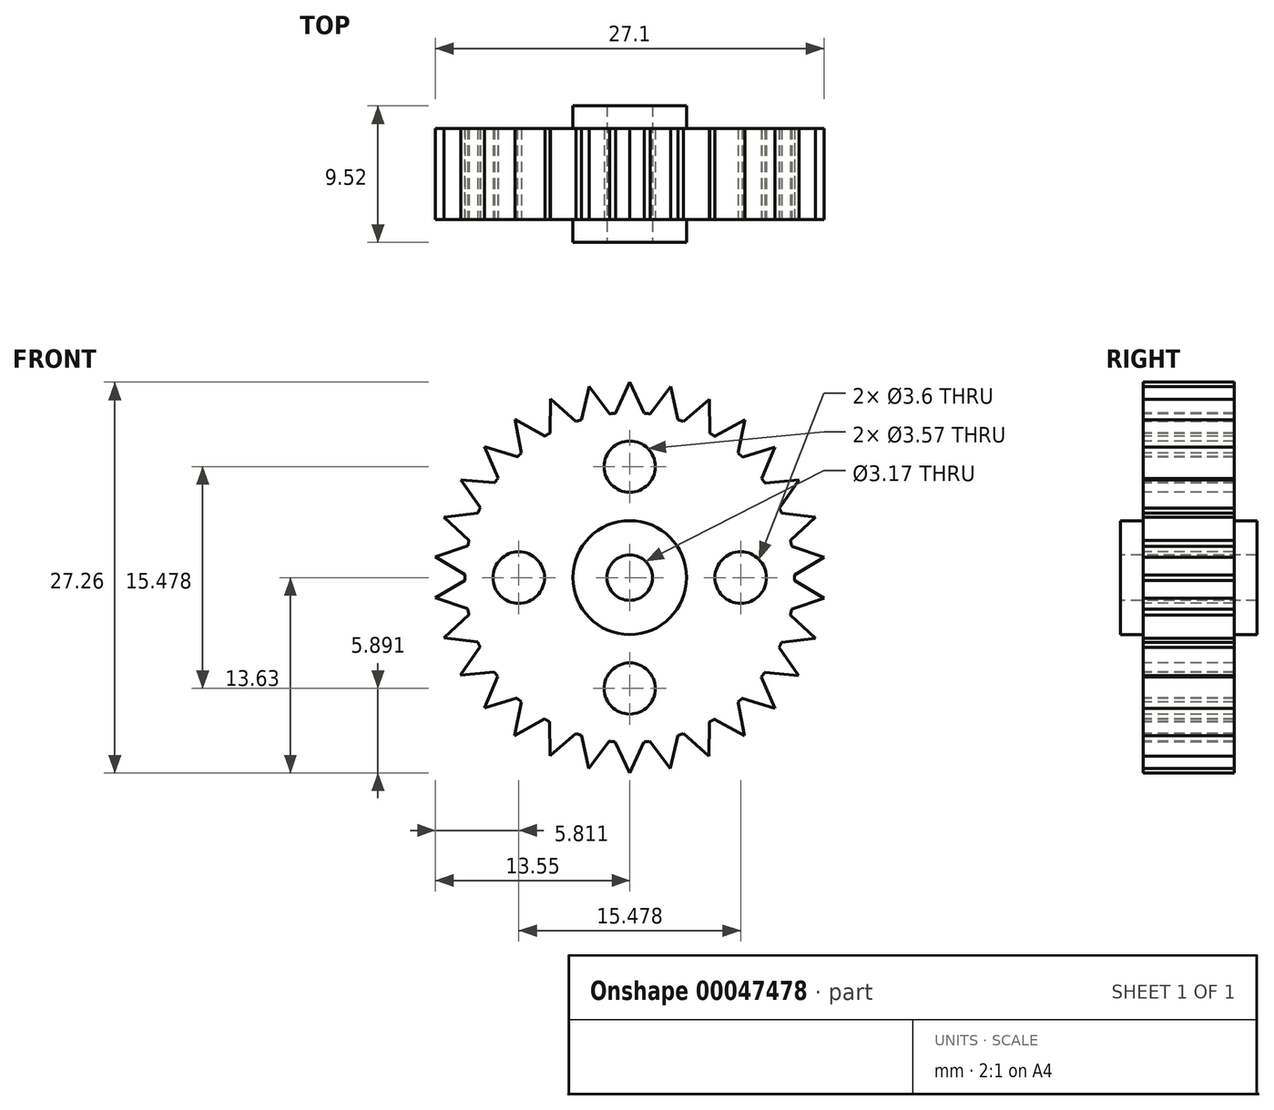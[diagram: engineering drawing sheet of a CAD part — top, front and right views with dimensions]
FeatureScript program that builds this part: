
annotation { "Feature Type Name" : "Feature", "Feature Type Description" : "" }
export const myFeature = defineFeature(function(context is Context, id is Id, definition is map)
    precondition{}
    {
        {
            var Q0;
            Q0=qCreatedBy(makeId("Front.planeOp"),FACE);
            var sketch = newSketch(context, id + "F0", { "sketchPlane" : qUnion([Q0])});
            skCircle(sketch, "E0", {"center": v(0, 0) * mm, "radius": 11.5 * mm});
            skSolve(sketch);
        }
        {
            var Q0;
            Q0=makeQuery(id+"F0.imprint","IMPRINT",FACE,{"disambiguationData":[TD([[makeQuery(id+"F0.imprint","IMPRINT",EDGE,{"derivedFrom":sQuery(id+"F0.wireOp",EDGE,"E0")}),1.0]])]});
            extrude(context, id + "F1", {"entities" : qUnion([Q0]), "depth" : 6.35 * mm, "symmetric" : true});
        }
        {
            var Q0;
            Q0=makeQuery(id+"F1.opExtrude","CAP_FACE",FACE,{"disambiguationData":[OSD([sQuery(id+"F0.wireOp",EDGE,"E0")])],"isStart":false});
            var sketch = newSketch(context, id + "F2", { "sketchPlane" : qUnion([Q0])});
            skCircle(sketch, "E1", {"center": v(0, 0) * mm, "radius": 3.97 * mm});
            skSolve(sketch);
        }
        {
            var Q0;
            Q0=makeQuery(id+"F2.imprint","IMPRINT",FACE,{"disambiguationData":[TD([[makeQuery(id+"F2.imprint","IMPRINT",EDGE,{"derivedFrom":sQuery(id+"F2.wireOp",EDGE,"E1")}),1.0]])]});
            extrude(context, id + "F3", {"entities" : qUnion([Q0]), "operationType" : NewBodyOperationType.ADD, "depth" : 1.59 * mm});
        }
        {
            var Q0;
            Q0=makeQuery(id+"F3.opExtrude","CAP_FACE",FACE,{"disambiguationData":[OSD([sQuery(id+"F2.wireOp",EDGE,"E1")])],"isStart":false});
            var sketch = newSketch(context, id + "F4", { "sketchPlane" : qUnion([Q0])});
            skCircle(sketch, "E2", {"center": v(0, 0) * mm, "radius": 1.59 * mm});
            skSolve(sketch);
        }
        {
            var Q0;
            Q0=makeQuery(id+"F4.imprint","IMPRINT",FACE,{"disambiguationData":[TD([[makeQuery(id+"F4.imprint","IMPRINT",EDGE,{"derivedFrom":sQuery(id+"F4.wireOp",EDGE,"E2")}),1.0]])]});
            extrude(context, id + "F5", {"entities" : qUnion([Q0]), "operationType" : NewBodyOperationType.REMOVE, "endBound" : BoundingType.THROUGH_ALL, "oppositeDirection" : true, "depth" : 25.4 * mm});
        }
        {
            var Q0;
            Q0=makeQuery(id+"F1.opExtrude","CAP_FACE",FACE,{"disambiguationData":[OSD([sQuery(id+"F0.wireOp",EDGE,"E0")])],"isStart":false});
            var sketch = newSketch(context, id + "F6", { "sketchPlane" : qUnion([Q0])});
            skCircle(sketch, "E3", {"center": v(0, 7.74) * mm, "radius": 1.79 * mm});
            skCircle(sketch, "E4.MirrorC", {"center": v(0, -7.74) * mm, "radius": 1.79 * mm});
            skCircle(sketch, "E5", {"center": v(-7.74, 0) * mm, "radius": 1.8 * mm});
            skCircle(sketch, "E6.MirrorC", {"center": v(7.74, 0) * mm, "radius": 1.8 * mm});
            skSolve(sketch);
        }
        {
            var Q0;
            Q0 = qSketchRegion(id + "F6", true);
            extrude(context, id + "F7", {"entities" : qUnion([Q0]), "operationType" : NewBodyOperationType.REMOVE, "endBound" : BoundingType.THROUGH_ALL, "oppositeDirection" : true, "depth" : 25.4 * mm});
        }
        {
            var Q0;
            Q0=makeQuery(id+"F1.opExtrude","CAP_FACE",FACE,{"disambiguationData":[OSD([sQuery(id+"F0.wireOp",EDGE,"E0")])],"isStart":false});
            var sketch = newSketch(context, id + "F8", { "sketchPlane" : qUnion([Q0])});
            skLineSegment(sketch, "E7", {"start": v(-1, 11.47) * mm, "end": v(0.01, 13.63) * mm});
            skLineSegment(sketch, "E8", {"start": v(0.01, 13.63) * mm, "end": v(1.01, 11.46) * mm});
            skArc(sketch, "E9.trimOffspring", {"start": v(1.01, 11.46) * mm, "mid": v(0.01, 11.5) * mm, "end": v(-1, 11.47) * mm});
            skSolve(sketch);
        }
        {
            var Q0;
            Q0 = qSketchRegion(id + "F8", true);
            var Q1;
            Q1=makeQuery(id+"F1.opExtrude","CAP_FACE",FACE,{"disambiguationData":[OSD([sQuery(id+"F0.wireOp",EDGE,"E0")])],"isStart":true});
            extrude(context, id + "F9", {"entities" : qUnion([Q0]), "endBound" : BoundingType.UP_TO_SURFACE, "oppositeDirection" : true, "endBoundEntityFace" : qUnion([Q1]), "depth" : 25.4 * mm});
        }
        {
            var Q0;
            Q0=makeQuery(id+"F9.opExtrude","SWEPT_BODY",BODY,{"disambiguationData":[OSD([sQuery(id+"F8.wireOp",EDGE,"E7"),sQuery(id+"F8.wireOp",EDGE,"E8"),sQuery(id+"F8.wireOp",EDGE,"E9.trimOffspring")])]});
            var Q1;
            Q1=makeQuery(id+"F1.opExtrude","CAP_EDGE",EDGE,{"disambiguationData":[OSD([sQuery(id+"F0.wireOp",EDGE,"E0")])],"isStart":false});
            circularPattern(context, id + "F10", {"entities" : qUnion([Q0]), "axis" : qUnion([Q1]), "angle" : 360 * degree, "instanceCount" : 30, "equalSpace" : true});
        }
        {
            var Q0;
            Q0=makeQuery(id+"F1.opExtrude","SWEPT_BODY",BODY,{"disambiguationData":[OSD([sQuery(id+"F0.wireOp",EDGE,"E0")])]});
            var Q1;
            Q1=qCreatedBy(makeId("Front.planeOp"),FACE);
            mirror(context, id + "F11", {"operationType" : NewBodyOperationType.ADD, "entities" : qUnion([Q0]), "mirrorPlane" : qUnion([Q1])});
        }
    });
